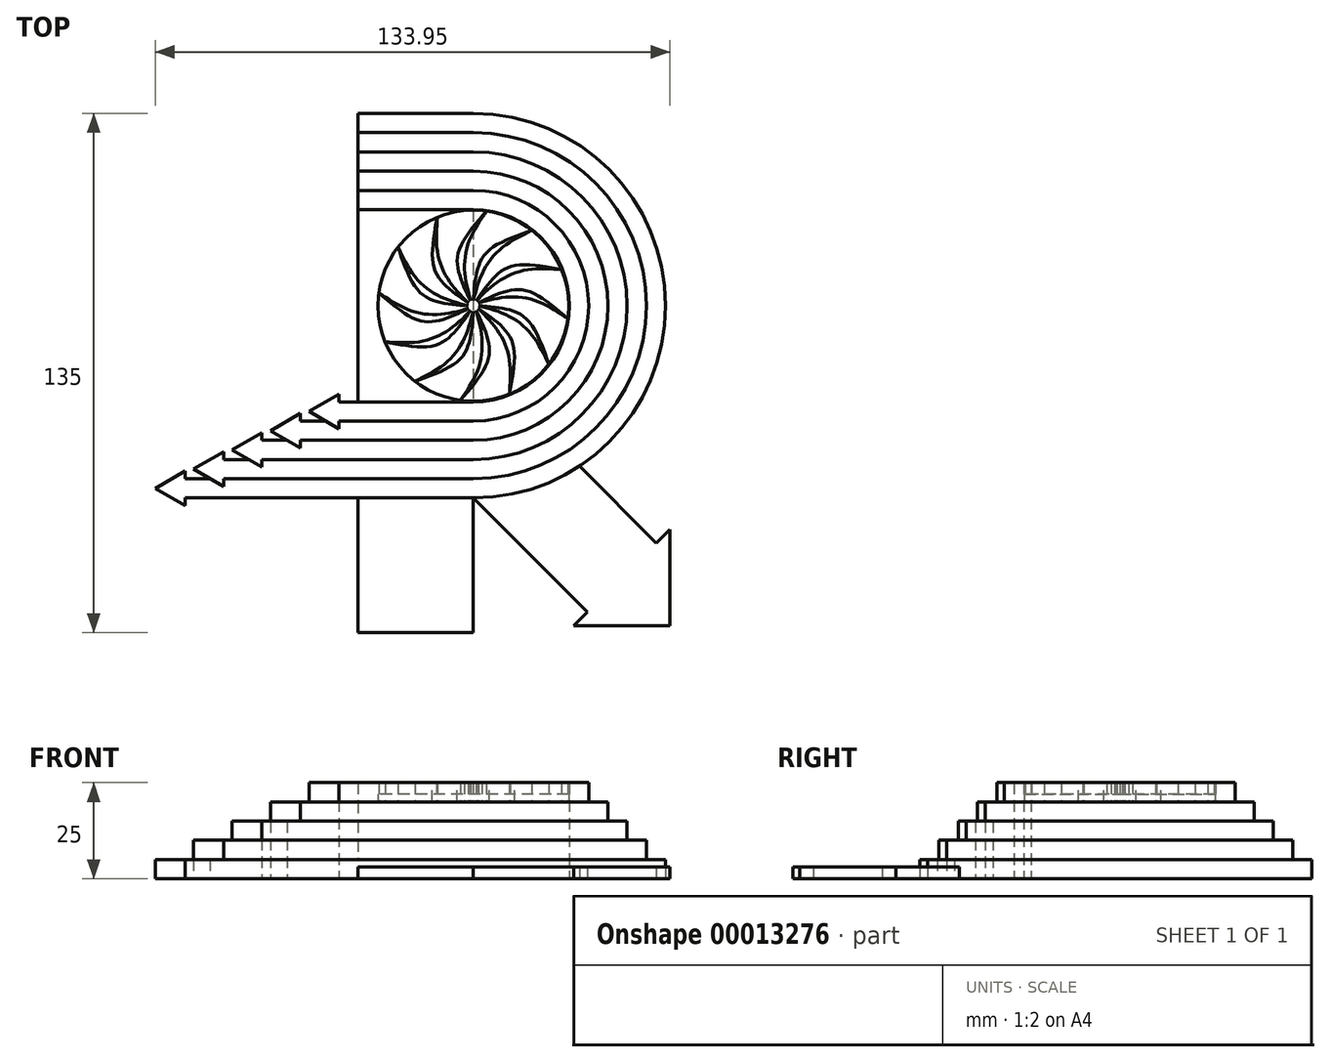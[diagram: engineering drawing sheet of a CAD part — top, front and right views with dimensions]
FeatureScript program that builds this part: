
annotation { "Feature Type Name" : "Feature", "Feature Type Description" : "" }
export const myFeature = defineFeature(function(context is Context, id is Id, definition is map)
    precondition{}
    {
        {
            var Q0;
            Q0=qCreatedBy(makeId("Top.planeOp"),FACE);
            var sketch = newSketch(context, id + "F0", { "sketchPlane" : qUnion([Q0])});
            skArc(sketch, "E0", {"start": v(0, -50) * mm, "mid": v(50, 0) * mm, "end": v(0, 50) * mm});
            skArc(sketch, "E1.0", {"start": v(0, -45) * mm, "mid": v(45, 0) * mm, "end": v(0, 45) * mm});
            skArc(sketch, "E2.0", {"start": v(0, -40) * mm, "mid": v(40, 0) * mm, "end": v(0, 40) * mm});
            skArc(sketch, "E3.0", {"start": v(0, -35) * mm, "mid": v(35, 0) * mm, "end": v(0, 35) * mm});
            skArc(sketch, "E4.0", {"start": v(0, -30) * mm, "mid": v(30, 0) * mm, "end": v(0, 30) * mm});
            skArc(sketch, "E5.0", {"start": v(0, -25) * mm, "mid": v(25, 0) * mm, "end": v(0, 25) * mm});
            skLineSegment(sketch, "E6", {"start": v(0, 0) * mm, "end": v(0, 50) * mm});
            skLineSegment(sketch, "E7", {"start": v(0, 0) * mm, "end": v(0, -85) * mm});
            skLineSegment(sketch, "E8.0", {"start": v(-30, 0) * mm, "end": v(-30, -85) * mm});
            skLineSegment(sketch, "E8.1", {"start": v(-30, 0) * mm, "end": v(-30, 50) * mm});
            skLineSegment(sketch, "E9", {"start": v(0, 50) * mm, "end": v(-30, 50) * mm});
            skLineSegment(sketch, "E10", {"start": v(0, 30) * mm, "end": v(-30, 30) * mm});
            skLineSegment(sketch, "E11", {"start": v(0, 35) * mm, "end": v(-30, 35) * mm});
            skLineSegment(sketch, "E12", {"start": v(0, 40) * mm, "end": v(-30, 40) * mm});
            skLineSegment(sketch, "E13", {"start": v(0, 45) * mm, "end": v(-30, 45) * mm});
            skLineSegment(sketch, "E14", {"start": v(0, -25) * mm, "end": v(-35, -25) * mm});
            skLineSegment(sketch, "E15", {"start": v(0, -30) * mm, "end": v(-35, -30) * mm});
            skLineSegment(sketch, "E16", {"start": v(0, -35) * mm, "end": v(-45, -35) * mm});
            skLineSegment(sketch, "E17", {"start": v(0, -40) * mm, "end": v(-55, -40) * mm});
            skLineSegment(sketch, "E18", {"start": v(0, -45) * mm, "end": v(-65, -45) * mm});
            skLineSegment(sketch, "E19", {"start": v(0, -50) * mm, "end": v(-75, -50) * mm});
            skLineSegment(sketch, "E20", {"start": v(-35, -23) * mm, "end": v(-35, -25) * mm});
            skLineSegment(sketch, "E21", {"start": v(-35, -32) * mm, "end": v(-42.8, -27.5) * mm});
            skLineSegment(sketch, "E22", {"start": v(-42.8, -27.5) * mm, "end": v(-35, -23) * mm});
            skLineSegment(sketch, "E23", {"start": v(-35, -30) * mm, "end": v(-35, -32) * mm});
            skLineSegment(sketch, "E24", {"start": v(0, 25) * mm, "end": v(-30, 25) * mm});
            skLineSegment(sketch, "E25", {"start": v(-45, -35) * mm, "end": v(-45, -37) * mm});
            skLineSegment(sketch, "E26", {"start": v(-45, -37) * mm, "end": v(-52.8, -32.5) * mm});
            skLineSegment(sketch, "E27", {"start": v(-52.8, -32.5) * mm, "end": v(-45, -28) * mm});
            skLineSegment(sketch, "E28", {"start": v(-45, -28) * mm, "end": v(-45, -30) * mm});
            skLineSegment(sketch, "E29", {"start": v(-45, -30) * mm, "end": v(-38.46, -30) * mm});
            skLineSegment(sketch, "E30", {"start": v(-55, -40) * mm, "end": v(-55, -42) * mm});
            skLineSegment(sketch, "E31", {"start": v(-55, -42) * mm, "end": v(-62.8, -37.5) * mm});
            skLineSegment(sketch, "E32", {"start": v(-62.8, -37.5) * mm, "end": v(-55, -33) * mm});
            skLineSegment(sketch, "E33", {"start": v(-55, -33) * mm, "end": v(-55, -35) * mm});
            skLineSegment(sketch, "E34", {"start": v(-55, -35) * mm, "end": v(-48.46, -35) * mm});
            skLineSegment(sketch, "E35", {"start": v(-65, -45) * mm, "end": v(-65, -47) * mm});
            skLineSegment(sketch, "E36", {"start": v(-65, -47) * mm, "end": v(-72.8, -42.5) * mm});
            skLineSegment(sketch, "E37", {"start": v(-72.8, -42.5) * mm, "end": v(-65, -38) * mm});
            skLineSegment(sketch, "E38", {"start": v(-65, -38) * mm, "end": v(-65, -40) * mm});
            skLineSegment(sketch, "E39", {"start": v(-65, -40) * mm, "end": v(-58.46, -40) * mm});
            skLineSegment(sketch, "E40", {"start": v(-75, -50) * mm, "end": v(-75, -52) * mm});
            skLineSegment(sketch, "E41", {"start": v(-75, -52) * mm, "end": v(-82.8, -47.5) * mm});
            skLineSegment(sketch, "E42", {"start": v(-82.8, -47.5) * mm, "end": v(-75, -43) * mm});
            skLineSegment(sketch, "E43", {"start": v(-75, -43) * mm, "end": v(-75, -45) * mm});
            skLineSegment(sketch, "E44", {"start": v(-75, -45) * mm, "end": v(-68.46, -45) * mm});
            skLineSegment(sketch, "E45", {"start": v(-30, -85) * mm, "end": v(0, -85) * mm});
            skLineSegment(sketch, "E46", {"start": v(0, -50) * mm, "end": v(29.7, -79.7) * mm});
            skLineSegment(sketch, "E47", {"start": v(29.7, -79.7) * mm, "end": v(26.16, -83.23) * mm});
            skLineSegment(sketch, "E48", {"start": v(26.16, -83.23) * mm, "end": v(51.16, -83.23) * mm});
            skLineSegment(sketch, "E49", {"start": v(51.16, -83.23) * mm, "end": v(51.16, -58.23) * mm});
            skLineSegment(sketch, "E50", {"start": v(51.16, -58.23) * mm, "end": v(47.63, -61.77) * mm});
            skLineSegment(sketch, "E51", {"start": v(47.63, -61.77) * mm, "end": v(27.57, -41.71) * mm});
            skSolve(sketch);
        }
        {
            var Q0;
            {var subQ1=sQuery(id+"F0.wireOp",EDGE,"E10");Q0=makeQuery(id+"F0.imprint","IMPRINT",FACE,{"disambiguationData":[TD([[makeQuery(id+"F0.imprint","IMPRINT",EDGE,{"derivedFrom":subQ1}),1.0]])]});}
            var Q1;
            {var subQ2=sQuery(id+"F0.wireOp",EDGE,"E4.0");Q1=makeQuery(id+"F0.imprint","IMPRINT",FACE,{"disambiguationData":[TD([[makeQuery(id+"F0.imprint","IMPRINT",EDGE,{"derivedFrom":subQ2}),1.0]])]});}
            var Q2;
            {var subQ1=sQuery(id+"F0.wireOp",EDGE,"E8.0");var subQ5=sQuery(id+"F0.wireOp",EDGE,"E14");var subQ6=makeQuery(id+"F0.imprint","INTERSECT",VERTEX,{"derivedFrom":[subQ1,subQ5]});Q2=makeQuery(id+"F0.imprint","IMPRINT",FACE,{"disambiguationData":[TD([[makeQuery(id+"F0.imprint","IMPRINT",EDGE,{"disambiguationData":[TD([[subQ6,-1.0]])],"derivedFrom":subQ1}),1.0]])]});}
            var Q3;
            {var subQ4=sQuery(id+"F0.wireOp",EDGE,"E20");Q3=makeQuery(id+"F0.imprint","IMPRINT",FACE,{"disambiguationData":[TD([[makeQuery(id+"F0.imprint","IMPRINT",EDGE,{"derivedFrom":subQ4}),-1.0]])]});}
            extrude(context, id + "F1", {"entities" : qUnion([Q0, Q1, Q2, Q3]), "depth" : 25 * mm});
        }
        {
            var Q0;
            {var subQ1=sQuery(id+"F0.wireOp",EDGE,"E10");Q0=makeQuery(id+"F0.imprint","IMPRINT",FACE,{"disambiguationData":[TD([[makeQuery(id+"F0.imprint","IMPRINT",EDGE,{"derivedFrom":subQ1}),-1.0]])]});}
            var Q1;
            {var subQ2=sQuery(id+"F0.wireOp",EDGE,"E3.0");Q1=makeQuery(id+"F0.imprint","IMPRINT",FACE,{"disambiguationData":[TD([[makeQuery(id+"F0.imprint","IMPRINT",EDGE,{"derivedFrom":subQ2}),1.0]])]});}
            var Q2;
            {var subQ1=sQuery(id+"F0.wireOp",EDGE,"E8.0");var subQ5=sQuery(id+"F0.wireOp",EDGE,"E15");var subQ6=makeQuery(id+"F0.imprint","INTERSECT",VERTEX,{"derivedFrom":[subQ1,subQ5]});Q2=makeQuery(id+"F0.imprint","IMPRINT",FACE,{"disambiguationData":[TD([[makeQuery(id+"F0.imprint","IMPRINT",EDGE,{"disambiguationData":[TD([[subQ6,-1.0]])],"derivedFrom":subQ1}),1.0]])]});}
            var Q3;
            {var subQ5=sQuery(id+"F0.wireOp",EDGE,"E23");Q3=makeQuery(id+"F0.imprint","IMPRINT",FACE,{"disambiguationData":[TD([[makeQuery(id+"F0.imprint","IMPRINT",EDGE,{"derivedFrom":subQ5}),1.0]])]});}
            extrude(context, id + "F2", {"entities" : qUnion([Q0, Q1, Q2, Q3]), "operationType" : NewBodyOperationType.ADD, "depth" : 20 * mm});
        }
        {
            var Q0;
            {var subQ6=sQuery(id+"F0.wireOp",EDGE,"E25");Q0=makeQuery(id+"F0.imprint","IMPRINT",FACE,{"disambiguationData":[TD([[makeQuery(id+"F0.imprint","IMPRINT",EDGE,{"derivedFrom":subQ6}),1.0]])]});}
            var Q1;
            {var subQ1=sQuery(id+"F0.wireOp",EDGE,"E8.0");var subQ5=sQuery(id+"F0.wireOp",EDGE,"E16");var subQ6=makeQuery(id+"F0.imprint","INTERSECT",VERTEX,{"derivedFrom":[subQ1,subQ5]});Q1=makeQuery(id+"F0.imprint","IMPRINT",FACE,{"disambiguationData":[TD([[makeQuery(id+"F0.imprint","IMPRINT",EDGE,{"disambiguationData":[TD([[subQ6,-1.0]])],"derivedFrom":subQ1}),1.0]])]});}
            var Q2;
            {var subQ2=sQuery(id+"F0.wireOp",EDGE,"E2.0");Q2=makeQuery(id+"F0.imprint","IMPRINT",FACE,{"disambiguationData":[TD([[makeQuery(id+"F0.imprint","IMPRINT",EDGE,{"derivedFrom":subQ2}),1.0]])]});}
            var Q3;
            {var subQ1=sQuery(id+"F0.wireOp",EDGE,"E11");Q3=makeQuery(id+"F0.imprint","IMPRINT",FACE,{"disambiguationData":[TD([[makeQuery(id+"F0.imprint","IMPRINT",EDGE,{"derivedFrom":subQ1}),-1.0]])]});}
            extrude(context, id + "F3", {"entities" : qUnion([Q0, Q1, Q2, Q3]), "operationType" : NewBodyOperationType.ADD, "depth" : 15 * mm});
        }
        {
            var Q0;
            {var subQ5=sQuery(id+"F0.wireOp",EDGE,"E30");Q0=makeQuery(id+"F0.imprint","IMPRINT",FACE,{"disambiguationData":[TD([[makeQuery(id+"F0.imprint","IMPRINT",EDGE,{"derivedFrom":subQ5}),1.0]])]});}
            var Q1;
            {var subQ1=sQuery(id+"F0.wireOp",EDGE,"E8.0");var subQ5=sQuery(id+"F0.wireOp",EDGE,"E17");var subQ6=makeQuery(id+"F0.imprint","INTERSECT",VERTEX,{"derivedFrom":[subQ1,subQ5]});Q1=makeQuery(id+"F0.imprint","IMPRINT",FACE,{"disambiguationData":[TD([[makeQuery(id+"F0.imprint","IMPRINT",EDGE,{"disambiguationData":[TD([[subQ6,-1.0]])],"derivedFrom":subQ1}),1.0]])]});}
            var Q2;
            {var subQ2=sQuery(id+"F0.wireOp",EDGE,"E1.0");Q2=makeQuery(id+"F0.imprint","IMPRINT",FACE,{"disambiguationData":[TD([[makeQuery(id+"F0.imprint","IMPRINT",EDGE,{"derivedFrom":subQ2}),1.0]])]});}
            var Q3;
            {var subQ1=sQuery(id+"F0.wireOp",EDGE,"E12");Q3=makeQuery(id+"F0.imprint","IMPRINT",FACE,{"disambiguationData":[TD([[makeQuery(id+"F0.imprint","IMPRINT",EDGE,{"derivedFrom":subQ1}),-1.0]])]});}
            extrude(context, id + "F4", {"entities" : qUnion([Q0, Q1, Q2, Q3]), "operationType" : NewBodyOperationType.ADD, "depth" : 10 * mm});
        }
        {
            var Q0;
            {var subQ3=sQuery(id+"F0.wireOp",EDGE,"E35");Q0=makeQuery(id+"F0.imprint","IMPRINT",FACE,{"disambiguationData":[TD([[makeQuery(id+"F0.imprint","IMPRINT",EDGE,{"derivedFrom":subQ3}),1.0]])]});}
            var Q1;
            {var subQ1=sQuery(id+"F0.wireOp",EDGE,"E8.0");var subQ5=sQuery(id+"F0.wireOp",EDGE,"E19");var subQ6=makeQuery(id+"F0.imprint","INTERSECT",VERTEX,{"derivedFrom":[subQ1,subQ5]});Q1=makeQuery(id+"F0.imprint","IMPRINT",FACE,{"disambiguationData":[TD([[makeQuery(id+"F0.imprint","IMPRINT",EDGE,{"disambiguationData":[TD([[subQ6,1.0]])],"derivedFrom":subQ1}),1.0]])]});}
            var Q2;
            {var subQ1=sQuery(id+"F0.wireOp",EDGE,"E1.0");Q2=makeQuery(id+"F0.imprint","IMPRINT",FACE,{"disambiguationData":[TD([[makeQuery(id+"F0.imprint","IMPRINT",EDGE,{"derivedFrom":subQ1}),-1.0]])]});}
            var Q3;
            {var subQ1=sQuery(id+"F0.wireOp",EDGE,"E9");Q3=makeQuery(id+"F0.imprint","IMPRINT",FACE,{"disambiguationData":[TD([[makeQuery(id+"F0.imprint","IMPRINT",EDGE,{"derivedFrom":subQ1}),1.0]])]});}
            extrude(context, id + "F5", {"entities" : qUnion([Q0, Q1, Q2, Q3]), "operationType" : NewBodyOperationType.ADD, "depth" : 5 * mm});
        }
        {
            var Q0;
            {var subQ7=sQuery(id+"F0.wireOp",EDGE,"E24");Q0=makeQuery(id+"F0.imprint","IMPRINT",FACE,{"disambiguationData":[TD([[makeQuery(id+"F0.imprint","IMPRINT",EDGE,{"derivedFrom":subQ7}),1.0]])]});}
            extrude(context, id + "F6", {"entities" : qUnion([Q0]), "operationType" : NewBodyOperationType.ADD, "depth" : 20 * mm});
        }
        {
            var Q0;
            {var subQ0=sQuery(id+"F0.wireOp",EDGE,"E45");Q0=makeQuery(id+"F0.imprint","IMPRINT",FACE,{"disambiguationData":[TD([[makeQuery(id+"F0.imprint","IMPRINT",EDGE,{"derivedFrom":subQ0}),1.0]])]});}
            extrude(context, id + "F7", {"entities" : qUnion([Q0]), "operationType" : NewBodyOperationType.ADD, "depth" : 3 * mm});
        }
        {
            var Q0;
            {var subQ1=sQuery(id+"F0.wireOp",EDGE,"E46");Q0=makeQuery(id+"F0.imprint","IMPRINT",FACE,{"disambiguationData":[TD([[makeQuery(id+"F0.imprint","IMPRINT",EDGE,{"derivedFrom":subQ1}),1.0]])]});}
            extrude(context, id + "F8", {"entities" : qUnion([Q0]), "operationType" : NewBodyOperationType.ADD, "depth" : 3 * mm});
        }
        {
            var Q0;
            Q0=makeQuery(id+"F6.opExtrude","SWEPT_FACE",FACE,{"disambiguationData":[OSD([sQuery(id+"F0.wireOp",EDGE,"E6"),sQuery(id+"F0.wireOp",EDGE,"E7")])]});
            var sketch = newSketch(context, id + "F9", { "sketchPlane" : qUnion([Q0])});
            skLineSegment(sketch, "E52", {"start": v(0, -2.47) * mm, "end": v(0, 34.57) * mm, "construction": true});
            skSolve(sketch);
        }
        {
            var Q0;
            Q0=makeQuery(id+"F6.opExtrude","CAP_FACE",FACE,{"disambiguationData":[OSD([sQuery(id+"F0.wireOp",EDGE,"E6"),sQuery(id+"F0.wireOp",EDGE,"E7"),sQuery(id+"F0.wireOp",EDGE,"E8.0"),sQuery(id+"F0.wireOp",EDGE,"E8.1"),sQuery(id+"F0.wireOp",EDGE,"E14"),sQuery(id+"F0.wireOp",EDGE,"E24")])],"isStart":false});
            var sketch = newSketch(context, id + "F10", { "sketchPlane" : qUnion([Q0])});
            skFitSpline(sketch, "E53", {"points": [v(0, -1.38) * mm, v(-2.54, -8.9) * mm, v(-7.77, -15.36) * mm, v(-15.2, -19.62) * mm], "startDerivative": vector(-5.83, -22.92) * mm, "endDerivative": vector(-20.05, -10.36) * mm});
            skFitSpline(sketch, "E54", {"points": [v(0, -1.38) * mm, v(-0.88, -8.67) * mm, v(-4.1, -14.47) * mm, v(-15.2, -19.62) * mm], "startDerivative": vector(-1.53, -23.74) * mm, "endDerivative": vector(-29.65, -10.44) * mm});
            skPoint(sketch, "E55.0", {"position": v(0, 0) * mm});
            skCircle(sketch, "E56", {"center": v(0, 0) * mm, "radius": 24.81 * mm});
            skSolve(sketch);
        }
        {
            var Q0;
            {var subQ3=sQuery(id+"F10.wireOp",EDGE,"E53");Q0=makeQuery(id+"F10.imprint","IMPRINT",FACE,{"disambiguationData":[TD([[makeQuery(id+"F10.imprint","IMPRINT",EDGE,{"derivedFrom":subQ3}),-1.0]])]});}
            var Q1;
            {var subQ0=makeQuery(id+"F6.opExtrude","CAP_EDGE",EDGE,{"disambiguationData":[OSD([sQuery(id+"F0.wireOp",EDGE,"E6"),sQuery(id+"F0.wireOp",EDGE,"E7")])],"isStart":false});var subQ1=sQuery(id+"F10.wireOp",EDGE,"34b4f147-719e-48b8-a0b2-25b8bdac7163");var subQ4=makeQuery(id+"F10.imprint","INTERSECT",VERTEX,{"disambiguationData":[OD(0.0)],"derivedFrom":[subQ0,subQ1]});Q1=makeQuery(id+"F10.imprint","IMPRINT",FACE,{"disambiguationData":[TD([[makeQuery(id+"F10.imprint","IMPRINT",EDGE,{"disambiguationData":[TD([[subQ4,1.0]])],"derivedFrom":subQ1}),1.0]])]});}
            var Q2;
            {var subQ4=sQuery(id+"F10.wireOp",EDGE,"E54");Q2=makeQuery(id+"F10.imprint","IMPRINT",FACE,{"disambiguationData":[TD([[makeQuery(id+"F10.imprint","IMPRINT",EDGE,{"derivedFrom":subQ4}),1.0]])]});}
            var Q3;
            Q3=makeQuery(id+"F10.imprint","IMPRINT",FACE,{"disambiguationData":[TD([[makeQuery(id+"F10.imprint","IMPRINT",EDGE,{"derivedFrom":sQuery(id+"F10.wireOp",EDGE,"E53")}),1.0]])]});
            var Q4;
            {var subQ0=makeQuery(id+"F6.opExtrude","CAP_EDGE",EDGE,{"disambiguationData":[OSD([sQuery(id+"F0.wireOp",EDGE,"E6"),sQuery(id+"F0.wireOp",EDGE,"E7")])],"isStart":false});var subQ1=sQuery(id+"F10.wireOp",EDGE,"E56");var subQ4=makeQuery(id+"F10.imprint","INTERSECT",VERTEX,{"disambiguationData":[OD(0.0)],"derivedFrom":[subQ0,subQ1]});Q4=makeQuery(id+"F10.imprint","IMPRINT",FACE,{"disambiguationData":[TD([[makeQuery(id+"F10.imprint","IMPRINT",EDGE,{"disambiguationData":[TD([[subQ4,1.0]])],"derivedFrom":subQ1}),1.0]])]});}
            extrude(context, id + "F11", {"entities" : qUnion([Q0, Q1, Q2, Q3, Q4]), "depth" : 2 * mm});
        }
        {
            var Q0;
            Q0=makeQuery(id+"F10.imprint","IMPRINT",FACE,{"disambiguationData":[TD([[makeQuery(id+"F10.imprint","IMPRINT",EDGE,{"derivedFrom":sQuery(id+"F10.wireOp",EDGE,"E53")}),1.0]])]});
            extrude(context, id + "F12", {"entities" : qUnion([Q0]), "depth" : 5 * mm});
        }
        {
            var Q0;
            Q0=makeQuery(id+"F12.opExtrude","SWEPT_BODY",BODY,{"disambiguationData":[OSD([sQuery(id+"F10.wireOp",EDGE,"E53"),sQuery(id+"F10.wireOp",EDGE,"E54")])]});
            var Q1;
            Q1=sQuery(id+"F9.wireOp",EDGE,"E52");
            circularPattern(context, id + "F13", {"entities" : qUnion([Q0]), "axis" : qUnion([Q1]), "angle" : 360 * degree, "instanceCount" : 12, "equalSpace" : true});
        }
    });
